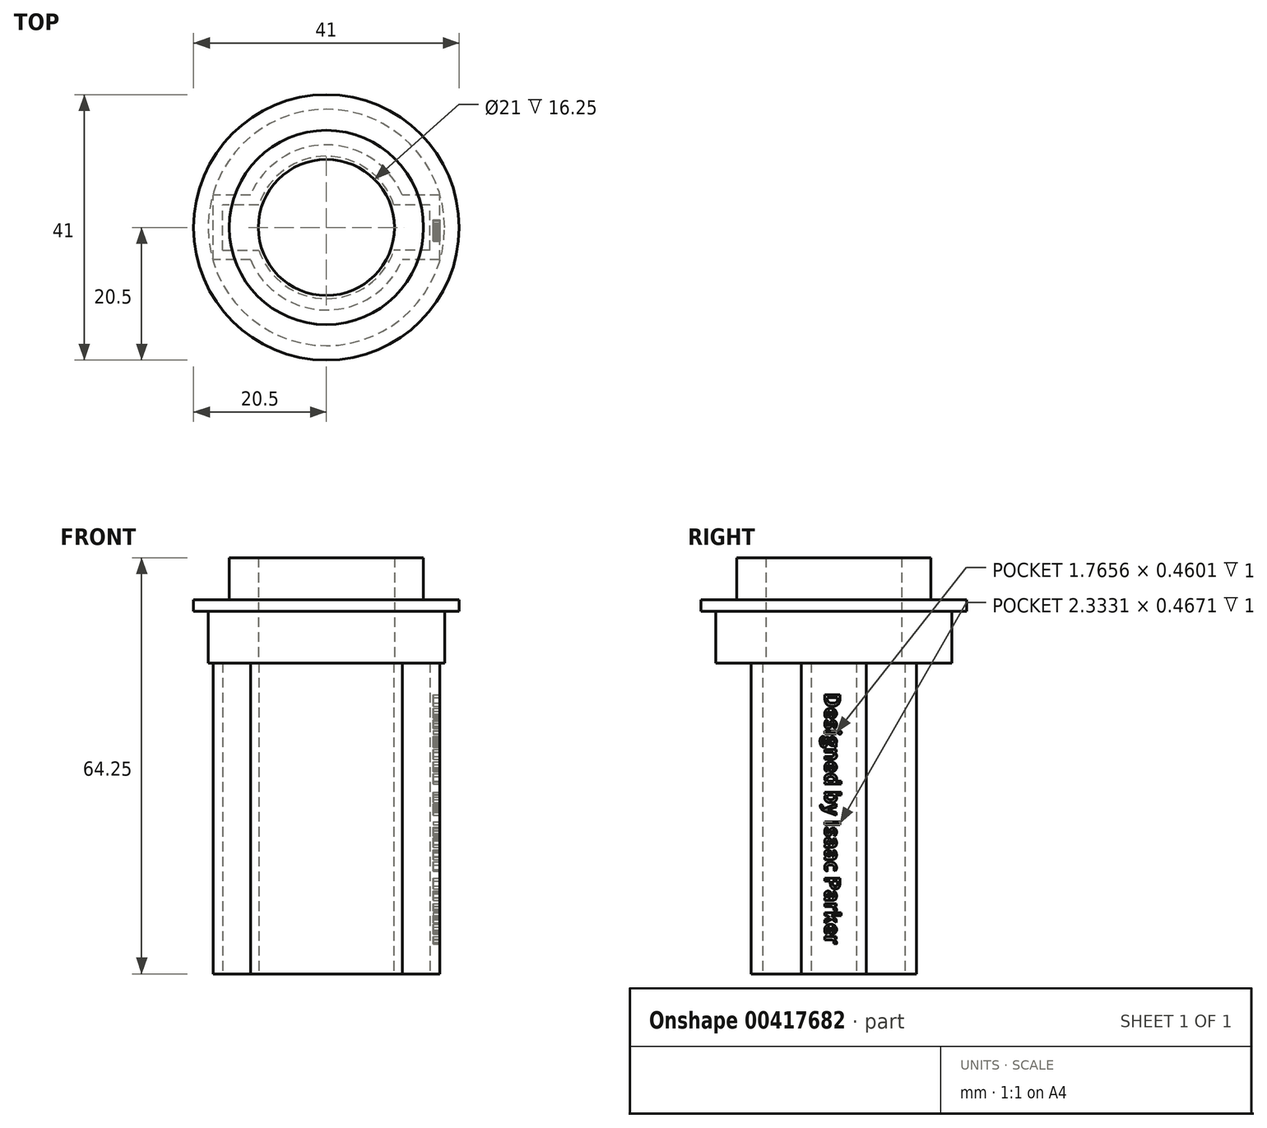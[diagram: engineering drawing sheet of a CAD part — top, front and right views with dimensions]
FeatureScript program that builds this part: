
annotation { "Feature Type Name" : "Feature", "Feature Type Description" : "" }
export const myFeature = defineFeature(function(context is Context, id is Id, definition is map)
    precondition{}
    {
        {
            var Q0;
            Q0=qCreatedBy(makeId("Top.planeOp"),FACE);
            var sketch = newSketch(context, id + "F0", { "sketchPlane" : qUnion([Q0])});
            skArc(sketch, "E0", {"start": v(-11.73, -5) * mm, "mid": v(0, -12.75) * mm, "end": v(11.73, -5) * mm});
            skArc(sketch, "E1", {"start": v(-10.43, -3.5) * mm, "mid": v(0, -11) * mm, "end": v(10.43, -3.5) * mm});
            skLineSegment(sketch, "E2.bottom", {"start": v(17.5, -5) * mm, "end": v(11.73, -5) * mm});
            skLineSegment(sketch, "E2.top", {"start": v(17.5, 5) * mm, "end": v(11.73, 5) * mm});
            skLineSegment(sketch, "E2.left", {"start": v(17.5, -5) * mm, "end": v(17.5, 5) * mm});
            skLineSegment(sketch, "E2.right", {"start": v(-17.5, -5) * mm, "end": v(-17.5, 5) * mm});
            skLineSegment(sketch, "E3.0", {"start": v(16, 3.5) * mm, "end": v(12.26, 3.5) * mm});
            skLineSegment(sketch, "E3.1", {"start": v(16, -3.5) * mm, "end": v(16, 3.5) * mm});
            skLineSegment(sketch, "E3.2", {"start": v(16, -3.5) * mm, "end": v(12.26, -3.5) * mm});
            skLineSegment(sketch, "E3.3", {"start": v(-16, -3.5) * mm, "end": v(-16, 3.5) * mm});
            skLineSegment(sketch, "E4.trimOffspring", {"start": v(-12.26, 3.5) * mm, "end": v(-16, 3.5) * mm});
            skLineSegment(sketch, "E5.trimOffspring", {"start": v(-12.26, -3.5) * mm, "end": v(-16, -3.5) * mm});
            skLineSegment(sketch, "E6", {"start": v(-12.26, 3.5) * mm, "end": v(-10.43, 3.5) * mm});
            skLineSegment(sketch, "E7", {"start": v(-12.26, -3.5) * mm, "end": v(-10.43, -3.5) * mm});
            skLineSegment(sketch, "E8", {"start": v(12.26, 3.5) * mm, "end": v(10.43, 3.5) * mm});
            skLineSegment(sketch, "E9", {"start": v(12.26, -3.5) * mm, "end": v(10.43, -3.5) * mm});
            skLineSegment(sketch, "E10.trimOffspring", {"start": v(-11.73, 5) * mm, "end": v(-17.5, 5) * mm});
            skArc(sketch, "E11.trimOffspring", {"start": v(11.73, 5) * mm, "mid": v(0, 12.75) * mm, "end": v(-11.73, 5) * mm});
            skArc(sketch, "E12.trimOffspring", {"start": v(10.43, 3.5) * mm, "mid": v(0, 11) * mm, "end": v(-10.43, 3.5) * mm});
            skLineSegment(sketch, "E13.trimOffspring", {"start": v(-11.73, -5) * mm, "end": v(-17.5, -5) * mm});
            skSolve(sketch);
        }
        {
            var Q0;
            Q0=makeQuery(id+"F0.imprint","IMPRINT",FACE,{"disambiguationData":[TD([[makeQuery(id+"F0.imprint","IMPRINT",EDGE,{"derivedFrom":sQuery(id+"F0.wireOp",EDGE,"E0")}),1.0]])]});
            extrude(context, id + "F1", {"entities" : qUnion([Q0]), "depth" : 48 * mm});
        }
        {
            var Q0;
            Q0=makeQuery(id+"F1.opExtrude","CAP_FACE",FACE,{"disambiguationData":[OSD([sQuery(id+"F0.wireOp",EDGE,"E0"),sQuery(id+"F0.wireOp",EDGE,"E1"),sQuery(id+"F0.wireOp",EDGE,"E2.bottom"),sQuery(id+"F0.wireOp",EDGE,"E2.top"),sQuery(id+"F0.wireOp",EDGE,"E2.left"),sQuery(id+"F0.wireOp",EDGE,"E2.right"),sQuery(id+"F0.wireOp",EDGE,"E3.0"),sQuery(id+"F0.wireOp",EDGE,"E3.1"),sQuery(id+"F0.wireOp",EDGE,"E3.2"),sQuery(id+"F0.wireOp",EDGE,"E3.3"),sQuery(id+"F0.wireOp",EDGE,"E4.trimOffspring"),sQuery(id+"F0.wireOp",EDGE,"E5.trimOffspring"),sQuery(id+"F0.wireOp",EDGE,"E6"),sQuery(id+"F0.wireOp",EDGE,"E7"),sQuery(id+"F0.wireOp",EDGE,"E8"),sQuery(id+"F0.wireOp",EDGE,"E9"),sQuery(id+"F0.wireOp",EDGE,"E10.trimOffspring"),sQuery(id+"F0.wireOp",EDGE,"E11.trimOffspring"),sQuery(id+"F0.wireOp",EDGE,"E12.trimOffspring"),sQuery(id+"F0.wireOp",EDGE,"E13.trimOffspring")])],"isStart":false});
            var sketch = newSketch(context, id + "F2", { "sketchPlane" : qUnion([Q0])});
            skCircle(sketch, "E14", {"center": v(0, 0) * mm, "radius": 18.25 * mm});
            skCircle(sketch, "E15", {"center": v(0, 0) * mm, "radius": 10.5 * mm});
            skSolve(sketch);
        }
        {
            var Q0;
            Q0 = qSketchRegion(id + "F2", true);
            extrude(context, id + "F3", {"entities" : qUnion([Q0]), "operationType" : NewBodyOperationType.ADD, "depth" : 8 * mm});
        }
        {
            var Q0;
            Q0=makeQuery(id+"F3.opExtrude","CAP_FACE",FACE,{"disambiguationData":[OSD([sQuery(id+"F2.wireOp",EDGE,"E14"),sQuery(id+"F2.wireOp",EDGE,"E15")])],"isStart":false});
            var sketch = newSketch(context, id + "F4", { "sketchPlane" : qUnion([Q0])});
            skCircle(sketch, "E16", {"center": v(0, 0) * mm, "radius": 20.5 * mm});
            skCircle(sketch, "E17", {"center": v(0, 0) * mm, "radius": 10.5 * mm});
            skSolve(sketch);
        }
        {
            var Q0;
            Q0 = qSketchRegion(id + "F4", true);
            var Q1;
            Q1=makeQuery(id+"F4.imprint","IMPRINT",FACE,{"disambiguationData":[TD([[makeQuery(id+"F4.imprint","IMPRINT",EDGE,{"derivedFrom":sQuery(id+"F4.wireOp",EDGE,"E17")}),-1.0]])]});
            extrude(context, id + "F5", {"entities" : qUnion([Q0, Q1]), "operationType" : NewBodyOperationType.ADD, "depth" : 1.75 * mm});
        }
        {
            var Q0;
            Q0=makeQuery(id+"F5.opExtrude","CAP_FACE",FACE,{"disambiguationData":[OSD([sQuery(id+"F4.wireOp",EDGE,"E16"),sQuery(id+"F4.wireOp",EDGE,"E17")])],"isStart":false});
            var sketch = newSketch(context, id + "F6", { "sketchPlane" : qUnion([Q0])});
            skCircle(sketch, "E18", {"center": v(0, 0) * mm, "radius": 15 * mm});
            skCircle(sketch, "E19", {"center": v(0, 0) * mm, "radius": 10.5 * mm});
            skSolve(sketch);
        }
        {
            var Q0;
            Q0=makeQuery(id+"F6.imprint","IMPRINT",FACE,{"disambiguationData":[TD([[makeQuery(id+"F6.imprint","IMPRINT",EDGE,{"derivedFrom":sQuery(id+"F6.wireOp",EDGE,"E18")}),1.0]])]});
            extrude(context, id + "F7", {"entities" : qUnion([Q0]), "operationType" : NewBodyOperationType.ADD, "depth" : 6.5 * mm});
        }
        {
            var Q0;
            Q0=makeQuery(id+"F1.opExtrude","SWEPT_FACE",FACE,{"disambiguationData":[OSD([sQuery(id+"F0.wireOp",EDGE,"E2.left")])]});
            var sketch = newSketch(context, id + "F8", { "sketchPlane" : qUnion([Q0])});
            skText(sketch, "E20", { "text": "Designed by Isaac Parker", "fontName": "NotoSansCJKsc-Bold.otf"});
            const initialGuessF8  = {"E20": [-0.00137, 0.0434, 0, -1, 0.00227]};
            skSetInitialGuess(sketch, initialGuessF8);
            skSolve(sketch);
        }
        {
            var Q0;
            Q0 = qSketchRegion(id + "F8", true);
            extrude(context, id + "F9", {"entities" : qUnion([Q0]), "operationType" : NewBodyOperationType.REMOVE, "oppositeDirection" : true, "depth" : 1 * mm});
        }
    });
